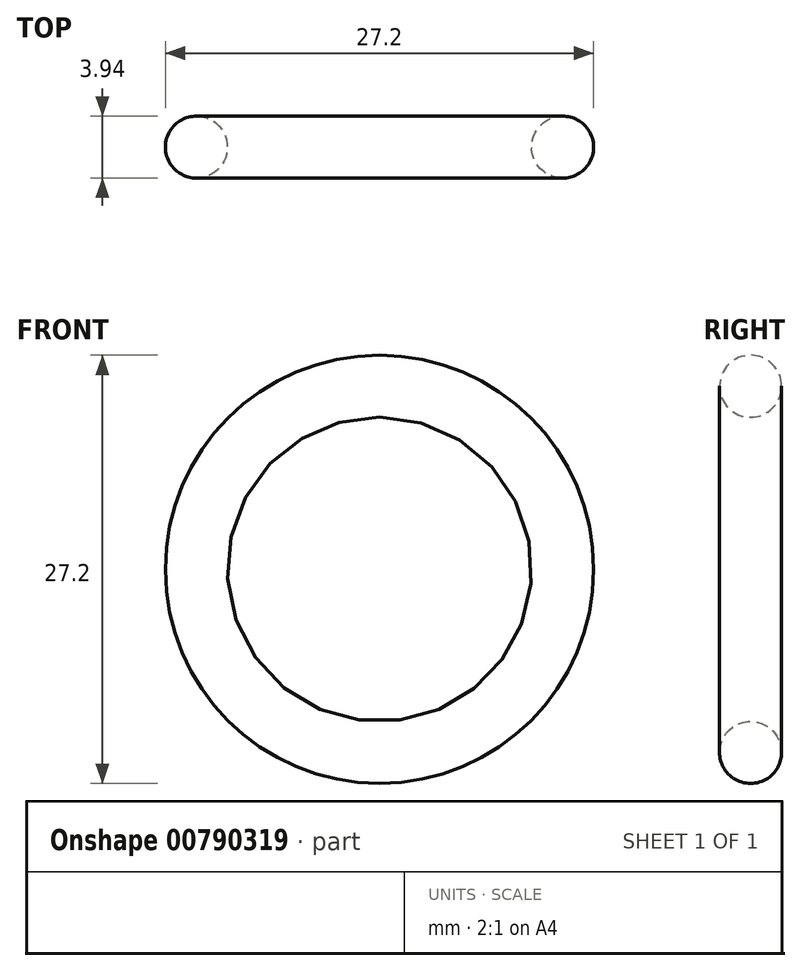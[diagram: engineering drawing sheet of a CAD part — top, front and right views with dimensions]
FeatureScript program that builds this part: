
annotation { "Feature Type Name" : "Feature", "Feature Type Description" : "" }
export const myFeature = defineFeature(function(context is Context, id is Id, definition is map)
    precondition{}
    {
        {
            var Q0;
            Q0=qCreatedBy(makeId("Front.planeOp"),FACE);
            var sketch = newSketch(context, id + "F0", { "sketchPlane" : qUnion([Q0])});
            skCircle(sketch, "E0", {"center": v(0, 0) * mm, "radius": 9.27 * mm});
            skSolve(sketch);
        }
        {
            var Q0;
            Q0=qCreatedBy(makeId("Top.planeOp"),FACE);
            var sketch = newSketch(context, id + "F1", { "sketchPlane" : qUnion([Q0])});
            skCircle(sketch, "E1", {"center": v(11.63, 0) * mm, "radius": 1.97 * mm});
            skSolve(sketch);
        }
        {
            var Q0;
            Q0=makeQuery(id+"F1.imprint","IMPRINT",FACE,{"disambiguationData":[TD([[makeQuery(id+"F1.imprint","IMPRINT",EDGE,{"derivedFrom":sQuery(id+"F1.wireOp",EDGE,"E1")}),1.0]])]});
            var Q1;
            Q1=sQuery(id+"F0.wireOp",EDGE,"E0");
            revolve(context, id + "F2", {"surfaceOperationType" : NewSurfaceOperationType.NEW, "entities" : qUnion([Q0]), "axis" : qUnion([Q1]), "revolveType" : RevolveType.FULL});
        }
    });
